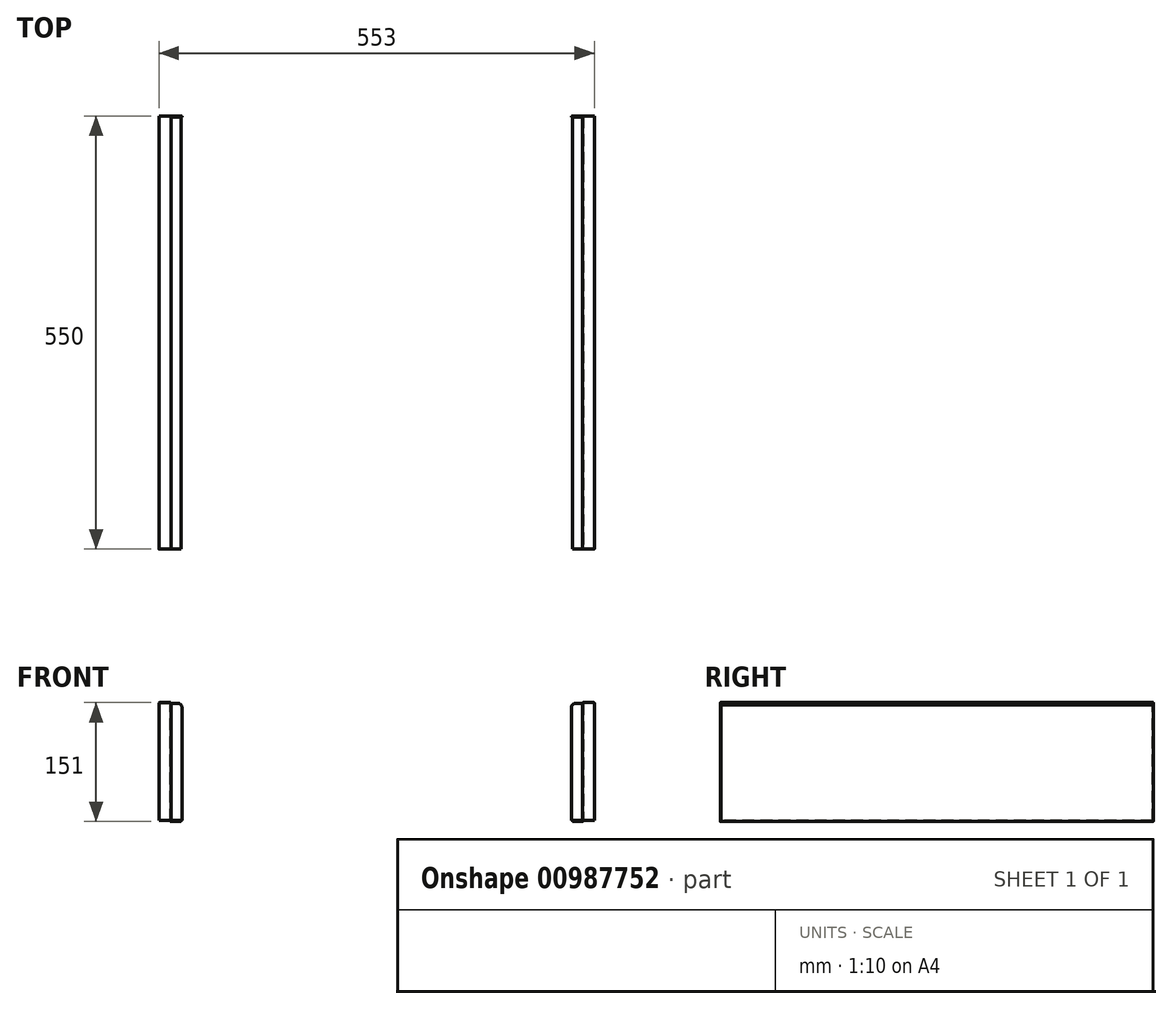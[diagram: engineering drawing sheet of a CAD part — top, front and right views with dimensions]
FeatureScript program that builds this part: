
annotation { "Feature Type Name" : "Feature", "Feature Type Description" : "" }
export const myFeature = defineFeature(function(context is Context, id is Id, definition is map)
    precondition{}
    {
        {
            var Q0;
            Q0=qCreatedBy(makeId("Front.planeOp"),FACE);
            var sketch = newSketch(context, id + "F0", { "sketchPlane" : qUnion([Q0])});
            skLineSegment(sketch, "E0.bottom", {"start": v(-275.5, 25.92) * mm, "end": v(-262.5, 25.92) * mm});
            skLineSegment(sketch, "E0.top", {"start": v(-261.5, -124.08) * mm, "end": v(-248.5, -124.08) * mm});
            skLineSegment(sketch, "E0.right", {"start": v(-262.5, 25.92) * mm, "end": v(-262.5, -123.08) * mm});
            skLineSegment(sketch, "E1", {"start": v(-275.5, 25.92) * mm, "end": v(-275.5, 23.92) * mm});
            skLineSegment(sketch, "E2.0", {"start": v(-16.41, -149972.58) * mm, "end": v(-10.6, -149972.58) * mm});
            skLineSegment(sketch, "E3", {"start": v(-275.5, 23.92) * mm, "end": v(-276.5, 23.92) * mm});
            skLineSegment(sketch, "E4", {"start": v(-276.5, 23.92) * mm, "end": v(-276.5, 25.92) * mm});
            skLineSegment(sketch, "E5", {"start": v(-275.5, 26.92) * mm, "end": v(-262.5, 26.92) * mm});
            skLineSegment(sketch, "E6", {"start": v(-261.5, 25.92) * mm, "end": v(-261.5, -123.08) * mm});
            skLineSegment(sketch, "E7", {"start": v(-261.5, -123.08) * mm, "end": v(-248.5, -123.08) * mm});
            skLineSegment(sketch, "E8", {"start": v(-248.5, -123.08) * mm, "end": v(-248.5, -124.08) * mm});
            skPoint(sketch, "E9.visualSharp", {"position": v(-276.5, 26.92) * mm});
            skArc(sketch, "E9.filletArc", {"start": v(-275.5, 26.92) * mm, "mid": v(-276.2, 26.63) * mm, "end": v(-276.5, 25.92) * mm});
            skPoint(sketch, "E10.visualSharp", {"position": v(-261.5, 26.92) * mm});
            skArc(sketch, "E10.filletArc", {"start": v(-261.5, 25.92) * mm, "mid": v(-261.8, 26.63) * mm, "end": v(-262.5, 26.92) * mm});
            skPoint(sketch, "E11.visualSharp", {"position": v(-262.5, -124.08) * mm});
            skArc(sketch, "E11.filletArc", {"start": v(-262.5, -123.08) * mm, "mid": v(-262.2, -123.79) * mm, "end": v(-261.5, -124.08) * mm});
            skSolve(sketch);
        }
        {
            var Q0;
            Q0=makeQuery(id+"F0.imprint","IMPRINT",FACE,{"disambiguationData":[TD([[makeQuery(id+"F0.imprint","IMPRINT",EDGE,{"derivedFrom":sQuery(id+"F0.wireOp",EDGE,"E0.bottom")}),1.0]])]});
            extrude(context, id + "F1", {"entities" : qUnion([Q0]), "oppositeDirection" : true, "depth" : 550 * mm, "offsetDistance" : 25 * mm});
        }
        {
            var Q0;
            Q0=makeQuery(id+"F1.opExtrude","SWEPT_FACE",FACE,{"disambiguationData":[OSD([sQuery(id+"F0.wireOp",EDGE,"E6")])]});
            var sketch = newSketch(context, id + "F2", { "sketchPlane" : qUnion([Q0])});
            skLineSegment(sketch, "E12.bottom", {"start": v(550, -123.08) * mm, "end": v(549, -123.08) * mm});
            skLineSegment(sketch, "E12.top", {"start": v(550, 25.92) * mm, "end": v(549, 25.92) * mm});
            skLineSegment(sketch, "E12.left", {"start": v(550, -123.08) * mm, "end": v(550, 25.92) * mm});
            skLineSegment(sketch, "E12.right", {"start": v(549, -123.08) * mm, "end": v(549, 25.92) * mm});
            skSolve(sketch);
        }
        {
            var Q0;
            Q0=qSketchRegion(id+"F2",true);
            extrude(context, id + "F3", {"entities" : qUnion([Q0]), "operationType" : NewBodyOperationType.ADD, "depth" : 14 * mm, "offsetDistance" : 25 * mm});
        }
        {
            var Q0;
            Q0=makeQuery(id+"F3.opExtrude","CAP_EDGE",EDGE,{"disambiguationData":[OSD([sQuery(id+"F2.wireOp",EDGE,"E12.top")])],"isStart":false});
            fillet(context, id + "F4", {"entities" : qUnion([Q0]), "radius" : 5 * mm, "tangentPropagation" : true, "allowEdgeOverflow" : false});
        }
        {
            var Q0;
            Q0=makeQuery(id+"F1.opExtrude","SWEPT_FACE",FACE,{"disambiguationData":[OSD([sQuery(id+"F0.wireOp",EDGE,"E0.right")])]});
            var sketch = newSketch(context, id + "F5", { "sketchPlane" : qUnion([Q0])});
            skLineSegment(sketch, "E13.bottom", {"start": v(0, -123.08) * mm, "end": v(-1, -123.08) * mm});
            skLineSegment(sketch, "E13.top", {"start": v(0, 25.92) * mm, "end": v(-1, 25.92) * mm});
            skLineSegment(sketch, "E13.left", {"start": v(0, -123.08) * mm, "end": v(0, 25.92) * mm});
            skLineSegment(sketch, "E13.right", {"start": v(-1, -123.08) * mm, "end": v(-1, 25.92) * mm});
            skSolve(sketch);
        }
        {
            var Q0;
            Q0=qSketchRegion(id+"F5",true);
            extrude(context, id + "F6", {"entities" : qUnion([Q0]), "operationType" : NewBodyOperationType.ADD, "depth" : 14 * mm, "offsetDistance" : 25 * mm});
        }
        {
            var Q0;
            Q0=qSketchRegion(id+"F5",true);
            extrude(context, id + "F7", {"entities" : qUnion([Q0]), "operationType" : NewBodyOperationType.ADD, "depth" : 14 * mm, "offsetDistance" : 25 * mm});
        }
        {
            var Q0;
            Q0=makeQuery(id+"F1.opExtrude","SWEPT_BODY",BODY,{"disambiguationData":[OSD([sQuery(id+"F0.wireOp",EDGE,"E0.bottom"),sQuery(id+"F0.wireOp",EDGE,"E0.top"),sQuery(id+"F0.wireOp",EDGE,"E0.right"),sQuery(id+"F0.wireOp",EDGE,"E1"),sQuery(id+"F0.wireOp",EDGE,"E3"),sQuery(id+"F0.wireOp",EDGE,"E4"),sQuery(id+"F0.wireOp",EDGE,"E5"),sQuery(id+"F0.wireOp",EDGE,"E6"),sQuery(id+"F0.wireOp",EDGE,"E7"),sQuery(id+"F0.wireOp",EDGE,"E8"),sQuery(id+"F0.wireOp",EDGE,"E9.filletArc"),sQuery(id+"F0.wireOp",EDGE,"E10.filletArc"),sQuery(id+"F0.wireOp",EDGE,"E11.filletArc")])]});
            var Q1;
            Q1=qCreatedBy(makeId("Right.planeOp"),FACE);
            mirror(context, id + "F8", {"entities" : qUnion([Q0]), "mirrorPlane" : qUnion([Q1])});
        }
    });
